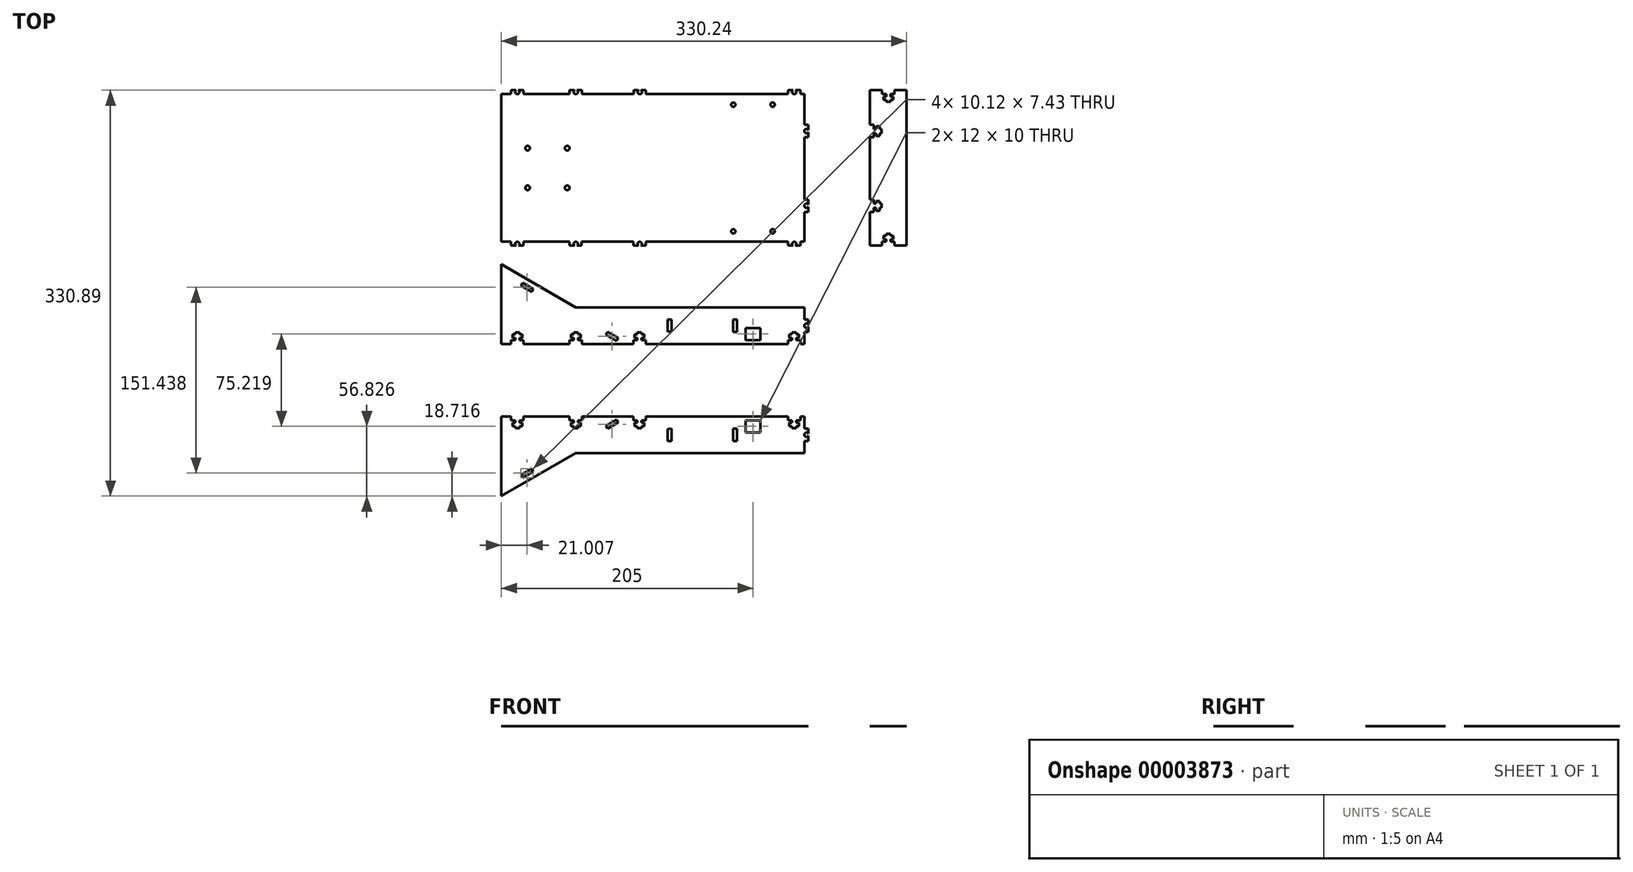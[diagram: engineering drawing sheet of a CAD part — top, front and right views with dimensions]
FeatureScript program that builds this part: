
annotation { "Feature Type Name" : "Feature", "Feature Type Description" : "" }
export const myFeature = defineFeature(function(context is Context, id is Id, definition is map)
    precondition{}
    {
        {
            var Q0;
            Q0=qCreatedBy(makeId("Top.planeOp"),FACE);
            var sketch = newSketch(context, id + "F0", { "sketchPlane" : qUnion([Q0])});
            skLineSegment(sketch, "E0", {"start": v(0, 40.15) * mm, "end": v(0, -39.56) * mm, "construction": true});
            skLineSegment(sketch, "E1", {"start": v(-52.6, 0) * mm, "end": v(51.5, 0) * mm, "construction": true});
            skLineSegment(sketch, "E2", {"start": v(-52.32, -7.62) * mm, "end": v(51.69, -7.62) * mm, "construction": true});
            skLineSegment(sketch, "E3", {"start": v(-7.62, 40.19) * mm, "end": v(-7.62, -39.92) * mm, "construction": true});
            skLineSegment(sketch, "E4", {"start": v(7.62, 39.74) * mm, "end": v(7.62, -40.14) * mm, "construction": true});
            skLineSegment(sketch, "E5", {"start": v(-52.6, 0) * mm, "end": v(-201.44, 0) * mm, "construction": true});
            skLineSegment(sketch, "E6", {"start": v(-52.32, -7.62) * mm, "end": v(-202.66, -7.62) * mm, "construction": true});
            skLineSegment(sketch, "E7", {"start": v(-13.97, 7.62) * mm, "end": v(-17.95, 7.62) * mm});
            skLineSegment(sketch, "E8", {"start": v(-257.62, 10.8) * mm, "end": v(-257.62, 131.12) * mm});
            skLineSegment(sketch, "E9", {"start": v(-7.62, 7.62) * mm, "end": v(-7.62, 10.8) * mm});
            skPoint(sketch, "E10", {"position": v(-97.62, 134.3) * mm});
            skPoint(sketch, "E11", {"position": v(-52.62, 134.3) * mm});
            skPoint(sketch, "E12", {"position": v(-46.62, 134.3) * mm});
            skPoint(sketch, "E13", {"position": v(-58.62, 134.3) * mm});
            skLineSegment(sketch, "E14", {"start": v(-202.66, -7.62) * mm, "end": v(-357.11, -7.62) * mm, "construction": true});
            skLineSegment(sketch, "E15", {"start": v(-201.44, 0) * mm, "end": v(-357.64, 0) * mm, "construction": true});
            skLineSegment(sketch, "E16", {"start": v(-7.62, -39.92) * mm, "end": v(-7.62, -62.62) * mm, "construction": true});
            skLineSegment(sketch, "E17", {"start": v(0, -39.56) * mm, "end": v(0, -201.8) * mm, "construction": true});
            skLineSegment(sketch, "E18", {"start": v(7.62, -40.14) * mm, "end": v(7.62, -202.84) * mm, "construction": true});
            skPoint(sketch, "E19.start.orphan", {"position": v(-257.62, -7.62) * mm});
            skLineSegment(sketch, "E20", {"start": v(-257.62, -7.62) * mm, "end": v(-257.62, -72.62) * mm, "construction": true});
            skLineSegment(sketch, "E21", {"start": v(-257.62, -72.62) * mm, "end": v(-145.04, -72.62) * mm, "construction": true});
            skLineSegment(sketch, "E22", {"start": v(-257.62, -7.62) * mm, "end": v(-197, -42.62) * mm});
            skLineSegment(sketch, "E23", {"start": v(-257.62, -7.62) * mm, "end": v(-257.62, -72.62) * mm});
            skPoint(sketch, "E24", {"position": v(-257.62, -72.62) * mm});
            skPoint(sketch, "E25", {"position": v(-257.62, -42.62) * mm});
            skLineSegment(sketch, "E26", {"start": v(-197, -42.62) * mm, "end": v(-10.8, -42.62) * mm});
            skLineSegment(sketch, "E27", {"start": v(-7.62, -52.62) * mm, "end": v(-7.62, -56.6) * mm});
            skPoint(sketch, "E28", {"position": v(-197, -42.62) * mm});
            skPoint(sketch, "E29", {"position": v(-197, -72.62) * mm});
            skPoint(sketch, "E30", {"position": v(-145.04, -72.62) * mm});
            skLineSegment(sketch, "E31", {"start": v(0, 0) * mm, "end": v(117.44, -117.44) * mm, "construction": true});
            skLineSegment(sketch, "E32", {"start": v(-7.62, -42.62) * mm, "end": v(42.62, -42.62) * mm, "construction": true});
            skLineSegment(sketch, "E33", {"start": v(-7.62, -72.62) * mm, "end": v(72.62, -72.62) * mm});
            skLineSegment(sketch, "E34", {"start": v(-7.62, 134.3) * mm, "end": v(110.23, 134.3) * mm, "construction": true});
            skLineSegment(sketch, "E35", {"start": v(42.62, -42.62) * mm, "end": v(42.62, 134.3) * mm, "construction": true});
            skLineSegment(sketch, "E36", {"start": v(72.62, -72.62) * mm, "end": v(72.62, 134.3) * mm, "construction": true});
            skLineSegment(sketch, "E37", {"start": v(72.62, 7.62) * mm, "end": v(72.62, 134.3) * mm});
            skLineSegment(sketch, "E38", {"start": v(-58.62, 134.3) * mm, "end": v(-58.62, -72.62) * mm, "construction": true});
            skLineSegment(sketch, "E39", {"start": v(-46.62, 134.3) * mm, "end": v(-46.62, -72.62) * mm, "construction": true});
            skPoint(sketch, "E40", {"position": v(-7.62, -57.62) * mm});
            skLineSegment(sketch, "E41", {"start": v(-7.62, -57.62) * mm, "end": v(57.62, -57.62) * mm, "construction": true});
            skLineSegment(sketch, "E42", {"start": v(57.62, -57.62) * mm, "end": v(57.62, 10.8) * mm, "construction": true});
            skPoint(sketch, "E43", {"position": v(-7.62, -52.62) * mm});
            skPoint(sketch, "E44", {"position": v(-7.62, -62.62) * mm});
            skLineSegment(sketch, "E45", {"start": v(-7.62, -52.62) * mm, "end": v(-58.62, -52.62) * mm, "construction": true});
            skLineSegment(sketch, "E46", {"start": v(-7.62, -62.62) * mm, "end": v(-58.62, -62.62) * mm, "construction": true});
            skLineSegment(sketch, "E47", {"start": v(-52.62, 134.3) * mm, "end": v(-52.62, -72.62) * mm, "construction": true});
            skPoint(sketch, "E48", {"position": v(-7.62, -67.62) * mm});
            skLineSegment(sketch, "E49", {"start": v(-7.62, -67.62) * mm, "end": v(-58.62, -67.62) * mm, "construction": true});
            skLineSegment(sketch, "E50", {"start": v(-58.62, -69.45) * mm, "end": v(-58.62, -62.62) * mm});
            skLineSegment(sketch, "E51", {"start": v(-46.62, -62.62) * mm, "end": v(-46.62, -69.45) * mm});
            skLineSegment(sketch, "E52.trimOffspring", {"start": v(-46.62, -72.62) * mm, "end": v(-23.97, -72.62) * mm});
            skLineSegment(sketch, "E53.trimOffspring", {"start": v(-46.62, -72.62) * mm, "end": v(-7.62, -72.62) * mm, "construction": true});
            skPoint(sketch, "E54", {"position": v(-257.62, 7.62) * mm});
            skPoint(sketch, "E55", {"position": v(-257.62, 10.8) * mm});
            skPoint(sketch, "E56", {"position": v(-257.62, 131.12) * mm});
            skLineSegment(sketch, "E57", {"start": v(-257.62, 10.8) * mm, "end": v(-249.62, 10.8) * mm});
            skPoint(sketch, "E58", {"position": v(-249.62, 131.22) * mm});
            skPoint(sketch, "E59", {"position": v(-239.62, 131.13) * mm});
            skPoint(sketch, "E60", {"position": v(-244.62, 131.21) * mm});
            skPoint(sketch, "E61.orphan", {"position": v(-257.62, 134.63) * mm});
            skLineSegment(sketch, "E62.trimOffspring", {"start": v(-58.62, 134.3) * mm, "end": v(-7.62, 134.3) * mm, "construction": true});
            skArc(sketch, "E63", {"start": v(-245.64, 134.39) * mm, "mid": v(-244.63, 131.21) * mm, "end": v(-243.6, 134.38) * mm});
            skArc(sketch, "E64", {"start": v(-143.9, 7.62) * mm, "mid": v(-144.93, 10.8) * mm, "end": v(-145.95, 7.62) * mm});
            skArc(sketch, "E65", {"start": v(-17.95, 7.62) * mm, "mid": v(-18.97, 10.8) * mm, "end": v(-20, 7.62) * mm});
            skArc(sketch, "E66", {"start": v(-243.6, 7.62) * mm, "mid": v(-244.62, 10.8) * mm, "end": v(-245.64, 7.62) * mm});
            skArc(sketch, "E67", {"start": v(-19.99, 134.3) * mm, "mid": v(-18.96, 131.13) * mm, "end": v(-17.94, 134.3) * mm});
            skArc(sketch, "E68", {"start": v(-145.8, 134.3) * mm, "mid": v(-144.78, 131.13) * mm, "end": v(-143.75, 134.3) * mm});
            skArc(sketch, "E69", {"start": v(-198.02, 134.3) * mm, "mid": v(-197, 131.13) * mm, "end": v(-195.97, 134.3) * mm});
            skPoint(sketch, "E70.start.orphan", {"position": v(-249.62, 134.4) * mm});
            skPoint(sketch, "E71", {"position": v(-197, 131.13) * mm});
            skLineSegment(sketch, "E72", {"start": v(-7.62, 131.13) * mm, "end": v(42.62, 131.13) * mm, "construction": true});
            skLineSegment(sketch, "E73", {"start": v(52.62, 131.13) * mm, "end": v(55.87, 131.13) * mm});
            skLineSegment(sketch, "E74", {"start": v(-195.97, 134.3) * mm, "end": v(-192, 134.3) * mm});
            skPoint(sketch, "E75", {"position": v(-144.78, 131.13) * mm});
            skLineSegment(sketch, "E76", {"start": v(-249.62, 134.4) * mm, "end": v(-245.64, 134.39) * mm});
            skLineSegment(sketch, "E77", {"start": v(-239.62, 131.13) * mm, "end": v(-239.62, 134.38) * mm});
            skLineSegment(sketch, "E78", {"start": v(-239.62, 134.38) * mm, "end": v(-243.6, 134.38) * mm});
            skLineSegment(sketch, "E79", {"start": v(-249.62, 131.22) * mm, "end": v(-249.62, 134.4) * mm});
            skPoint(sketch, "E80", {"position": v(-249.62, 132.8) * mm});
            skLineSegment(sketch, "E81.trimOffspring", {"start": v(-243.6, 134.38) * mm, "end": v(-239.62, 134.38) * mm});
            skLineSegment(sketch, "E82.trimOffspring", {"start": v(-245.64, 134.39) * mm, "end": v(-249.62, 134.4) * mm});
            skPoint(sketch, "E83", {"position": v(-192, 131.25) * mm});
            skPoint(sketch, "E84", {"position": v(-202, 131.13) * mm});
            skLineSegment(sketch, "E85", {"start": v(-192, 131.25) * mm, "end": v(-192, 134.3) * mm});
            skLineSegment(sketch, "E86", {"start": v(-192, 134.3) * mm, "end": v(-195.97, 134.3) * mm});
            skLineSegment(sketch, "E87", {"start": v(-202, 131.13) * mm, "end": v(-202, 134.3) * mm});
            skLineSegment(sketch, "E88", {"start": v(-202, 134.3) * mm, "end": v(-198.02, 134.3) * mm});
            skLineSegment(sketch, "E89", {"start": v(-197, 132.88) * mm, "end": v(-197, 132.88) * mm});
            skLineSegment(sketch, "E90.trimOffspring", {"start": v(-197, 132.88) * mm, "end": v(-197, 134.3) * mm, "construction": true});
            skPoint(sketch, "E91", {"position": v(-13.97, 131.13) * mm});
            skPoint(sketch, "E92", {"position": v(-23.97, 131.13) * mm});
            skPoint(sketch, "E93", {"position": v(-18.97, 131.13) * mm});
            skLineSegment(sketch, "E94", {"start": v(-23.97, 131.13) * mm, "end": v(-23.97, 134.3) * mm});
            skLineSegment(sketch, "E95", {"start": v(-13.97, 131.13) * mm, "end": v(-13.97, 134.3) * mm});
            skLineSegment(sketch, "E96", {"start": v(-23.97, 134.3) * mm, "end": v(-19.99, 134.3) * mm});
            skLineSegment(sketch, "E97.trimOffspring", {"start": v(-17.94, 134.3) * mm, "end": v(-13.97, 134.3) * mm});
            skPoint(sketch, "E98", {"position": v(-149.78, 131.16) * mm});
            skPoint(sketch, "E99", {"position": v(-139.78, 131.13) * mm});
            skLineSegment(sketch, "E100", {"start": v(-149.78, 131.16) * mm, "end": v(-149.78, 134.3) * mm});
            skLineSegment(sketch, "E101", {"start": v(-139.78, 131.13) * mm, "end": v(-139.78, 134.3) * mm});
            skLineSegment(sketch, "E102", {"start": v(-139.78, 134.3) * mm, "end": v(-143.75, 134.3) * mm});
            skLineSegment(sketch, "E103.trimOffspring", {"start": v(-145.8, 134.3) * mm, "end": v(-149.78, 134.3) * mm});
            skLineSegment(sketch, "E104", {"start": v(-143.75, 134.3) * mm, "end": v(-139.78, 134.3) * mm});
            skLineSegment(sketch, "E105", {"start": v(-139.78, 134.3) * mm, "end": v(-139.78, 131.13) * mm});
            skPoint(sketch, "E106", {"position": v(-145.8, 134.3) * mm});
            skPoint(sketch, "E107", {"position": v(-143.75, 134.3) * mm});
            skPoint(sketch, "E108.end.orphan", {"position": v(-144.77, 134.3) * mm});
            skLineSegment(sketch, "E109", {"start": v(-257.62, 131.12) * mm, "end": v(-249.62, 131.22) * mm});
            skLineSegment(sketch, "E110", {"start": v(-239.62, 131.13) * mm, "end": v(-202, 131.13) * mm});
            skLineSegment(sketch, "E111", {"start": v(-192, 131.25) * mm, "end": v(-149.78, 131.16) * mm});
            skLineSegment(sketch, "E112", {"start": v(-139.78, 131.13) * mm, "end": v(-23.97, 131.13) * mm});
            skLineSegment(sketch, "E113", {"start": v(-13.97, 131.13) * mm, "end": v(-10.8, 131.13) * mm});
            skLineSegment(sketch, "E114", {"start": v(-249.62, 7.62) * mm, "end": v(-249.62, 10.8) * mm});
            skLineSegment(sketch, "E115", {"start": v(-249.62, 7.62) * mm, "end": v(-245.64, 7.62) * mm});
            skLineSegment(sketch, "E116", {"start": v(-239.62, 7.62) * mm, "end": v(-239.62, 10.8) * mm});
            skLineSegment(sketch, "E117.trimOffspring", {"start": v(-239.62, 10.8) * mm, "end": v(-202, 10.8) * mm});
            skLineSegment(sketch, "E118", {"start": v(-202, 7.62) * mm, "end": v(-198.02, 7.62) * mm});
            skLineSegment(sketch, "E119", {"start": v(-202, 7.62) * mm, "end": v(-202, 10.8) * mm});
            skLineSegment(sketch, "E120.trimOffspring", {"start": v(-239.62, 7.62) * mm, "end": v(-243.6, 7.62) * mm});
            skLineSegment(sketch, "E121", {"start": v(-192.26, 7.62) * mm, "end": v(-192.25, 10.8) * mm});
            skLineSegment(sketch, "E122.trimOffspring", {"start": v(-192.25, 10.8) * mm, "end": v(-150.03, 10.8) * mm});
            skLineSegment(sketch, "E123", {"start": v(-150.04, 7.62) * mm, "end": v(-150.03, 10.8) * mm});
            skLineSegment(sketch, "E124", {"start": v(-139.78, 7.62) * mm, "end": v(-139.78, 10.8) * mm});
            skLineSegment(sketch, "E125.trimOffspring", {"start": v(-192.26, 7.62) * mm, "end": v(-195.97, 7.62) * mm});
            skLineSegment(sketch, "E126.trimOffspring", {"start": v(-139.78, 10.8) * mm, "end": v(-58.62, 10.8) * mm});
            skLineSegment(sketch, "E127.trimOffspring", {"start": v(-52.62, 10.8) * mm, "end": v(-7.62, 10.8) * mm});
            skLineSegment(sketch, "E128", {"start": v(-58.62, 10.8) * mm, "end": v(-46.62, 10.8) * mm});
            skLineSegment(sketch, "E129.trimOffspring", {"start": v(-52.23, 7.62) * mm, "end": v(-52.62, 7.62) * mm});
            skLineSegment(sketch, "E130", {"start": v(-23.97, 7.62) * mm, "end": v(-23.97, 10.8) * mm});
            skLineSegment(sketch, "E131", {"start": v(-13.97, 7.62) * mm, "end": v(-13.97, 10.8) * mm});
            skPoint(sketch, "E132", {"position": v(-18.97, 10.8) * mm});
            skLineSegment(sketch, "E133", {"start": v(-144.93, 9.04) * mm, "end": v(-144.93, 7.29) * mm});
            skPoint(sketch, "E134", {"position": v(-244.62, 10.8) * mm});
            skLineSegment(sketch, "E135.trimOffspring", {"start": v(-245.64, 7.62) * mm, "end": v(-249.62, 7.62) * mm});
            skLineSegment(sketch, "E136.trimOffspring", {"start": v(-243.6, 7.62) * mm, "end": v(-239.62, 7.62) * mm});
            skLineSegment(sketch, "E137", {"start": v(-144.93, 9.04) * mm, "end": v(-144.93, 10.8) * mm});
            skArc(sketch, "E138", {"start": v(-195.97, 7.62) * mm, "mid": v(-197, 10.8) * mm, "end": v(-198.02, 7.62) * mm});
            skArc(sketch, "E139", {"start": v(-7.62, 41.22) * mm, "mid": v(-10.8, 40.2) * mm, "end": v(-7.62, 39.17) * mm});
            skArc(sketch, "E140", {"start": v(-7.62, -56.6) * mm, "mid": v(-10.8, -57.62) * mm, "end": v(-7.62, -58.64) * mm});
            skArc(sketch, "E141", {"start": v(-7.62, 102.07) * mm, "mid": v(-10.8, 101.04) * mm, "end": v(-7.62, 100.02) * mm});
            skLineSegment(sketch, "E142.trimOffspring", {"start": v(-198.02, 7.62) * mm, "end": v(-202, 7.62) * mm});
            skLineSegment(sketch, "E143.trimOffspring", {"start": v(-195.97, 7.62) * mm, "end": v(-192.26, 7.62) * mm});
            skLineSegment(sketch, "E144.trimOffspring", {"start": v(-144.93, 7.62) * mm, "end": v(-144.93, 7.62) * mm});
            skLineSegment(sketch, "E145.trimOffspring", {"start": v(-143.9, 7.62) * mm, "end": v(-139.78, 7.62) * mm});
            skArc(sketch, "E146.trimOffspring", {"start": v(-144.93, 7.29) * mm, "mid": v(-144.93, 7.29) * mm, "end": v(-144.93, 7.29) * mm});
            skLineSegment(sketch, "E147", {"start": v(-150.04, 7.62) * mm, "end": v(-145.95, 7.62) * mm});
            skLineSegment(sketch, "E148.trimOffspring", {"start": v(-20, 7.62) * mm, "end": v(-23.97, 7.62) * mm});
            skLineSegment(sketch, "E149.trimOffspring", {"start": v(-18.97, 7.62) * mm, "end": v(-13.97, 7.62) * mm});
            skPoint(sketch, "E150", {"position": v(-10.8, 131.13) * mm});
            skLineSegment(sketch, "E151", {"start": v(-10.8, 131.13) * mm, "end": v(-10.8, 10.8) * mm});
            skPoint(sketch, "E152", {"position": v(-257.62, 40.88) * mm});
            skPoint(sketch, "E153", {"position": v(-257.7, 70.96) * mm});
            skPoint(sketch, "E154", {"position": v(-257.62, 101.04) * mm});
            skLineSegment(sketch, "E155", {"start": v(-7.62, 40.19) * mm, "end": v(42.62, 39.91) * mm, "construction": true});
            skPoint(sketch, "E156", {"position": v(-7.62, 106.04) * mm});
            skPoint(sketch, "E157", {"position": v(-7.62, 96.04) * mm});
            skLineSegment(sketch, "E158", {"start": v(-7.62, 106.04) * mm, "end": v(-10.8, 106.04) * mm});
            skLineSegment(sketch, "E159", {"start": v(-7.62, 96.04) * mm, "end": v(-10.8, 96.04) * mm});
            skPoint(sketch, "E160", {"position": v(-7.62, 45.19) * mm});
            skPoint(sketch, "E161", {"position": v(-7.62, 101.04) * mm});
            skPoint(sketch, "E162", {"position": v(-7.62, 35.19) * mm});
            skLineSegment(sketch, "E163", {"start": v(-7.62, 45.19) * mm, "end": v(-10.8, 45.19) * mm});
            skLineSegment(sketch, "E164", {"start": v(-7.62, 35.19) * mm, "end": v(-10.8, 35.19) * mm});
            skPoint(sketch, "E165", {"position": v(-10.8, 45.19) * mm});
            skPoint(sketch, "E166", {"position": v(-10.8, 35.19) * mm});
            skPoint(sketch, "E167", {"position": v(-10.8, 101.04) * mm});
            skLineSegment(sketch, "E168.trimOffspring", {"start": v(-7.62, 96.04) * mm, "end": v(-7.62, 100.02) * mm});
            skLineSegment(sketch, "E169.trimOffspring", {"start": v(-7.62, 35.19) * mm, "end": v(-7.62, 39.17) * mm});
            skLineSegment(sketch, "E170.trimOffspring", {"start": v(-7.62, 102.07) * mm, "end": v(-7.62, 106.04) * mm});
            skLineSegment(sketch, "E171.trimOffspring", {"start": v(-7.62, 41.22) * mm, "end": v(-7.62, 45.19) * mm});
            skLineSegment(sketch, "E172", {"start": v(-144.78, 132.88) * mm, "end": v(-143.02, 132.88) * mm, "construction": true});
            skLineSegment(sketch, "E173", {"start": v(-144.78, 132.88) * mm, "end": v(-146.53, 132.88) * mm, "construction": true});
            skLineSegment(sketch, "E174", {"start": v(-18.97, 7.62) * mm, "end": v(-18.97, -7.62) * mm, "construction": true});
            skLineSegment(sketch, "E175", {"start": v(-18.97, -7.62) * mm, "end": v(-18.97, -42.62) * mm, "construction": true});
            skLineSegment(sketch, "E176", {"start": v(-18.97, -42.62) * mm, "end": v(-18.97, -72.62) * mm, "construction": true});
            skLineSegment(sketch, "E177", {"start": v(-197, 9.04) * mm, "end": v(-198.75, 9.04) * mm, "construction": true});
            skLineSegment(sketch, "E178", {"start": v(-197, 9.04) * mm, "end": v(-195.25, 9.04) * mm, "construction": true});
            skLineSegment(sketch, "E179", {"start": v(-195.25, 9.04) * mm, "end": v(-195.25, -72.62) * mm, "construction": true});
            skLineSegment(sketch, "E180", {"start": v(-198.75, 9.04) * mm, "end": v(-198.75, -64.68) * mm, "construction": true});
            skLineSegment(sketch, "E181", {"start": v(-244.62, 9.04) * mm, "end": v(-242.87, 9.04) * mm, "construction": true});
            skLineSegment(sketch, "E182", {"start": v(-244.62, 9.04) * mm, "end": v(-246.37, 9.04) * mm, "construction": true});
            skLineSegment(sketch, "E183", {"start": v(-242.87, 9.04) * mm, "end": v(-242.87, -72.62) * mm, "construction": true});
            skLineSegment(sketch, "E184", {"start": v(-244.62, 7.62) * mm, "end": v(-244.62, -67.46) * mm, "construction": true});
            skLineSegment(sketch, "E185", {"start": v(-246.37, 9.04) * mm, "end": v(-246.37, -72.62) * mm, "construction": true});
            skLineSegment(sketch, "E186", {"start": v(-202, 7.62) * mm, "end": v(-202, -63.1) * mm, "construction": true});
            skLineSegment(sketch, "E187", {"start": v(-150.04, 7.62) * mm, "end": v(-150.04, -72.62) * mm, "construction": true});
            skLineSegment(sketch, "E188", {"start": v(-144.93, 9.04) * mm, "end": v(-143.18, 9.04) * mm, "construction": true});
            skLineSegment(sketch, "E189", {"start": v(-144.93, 9.04) * mm, "end": v(-146.68, 9.04) * mm, "construction": true});
            skPoint(sketch, "E190", {"position": v(-143.25, -42.62) * mm});
            skPoint(sketch, "E191", {"position": v(-145, -42.62) * mm});
            skPoint(sketch, "E192", {"position": v(-146.75, -42.62) * mm});
            skLineSegment(sketch, "E193", {"start": v(-143.25, -42.62) * mm, "end": v(-143.28, -72.62) * mm, "construction": true});
            skLineSegment(sketch, "E194", {"start": v(-146.75, -42.62) * mm, "end": v(-146.75, -72.62) * mm, "construction": true});
            skLineSegment(sketch, "E195", {"start": v(-18.97, 9.04) * mm, "end": v(-17.22, 9.04) * mm, "construction": true});
            skLineSegment(sketch, "E196", {"start": v(-18.97, 9.04) * mm, "end": v(-20.72, 9.04) * mm, "construction": true});
            skLineSegment(sketch, "E197", {"start": v(-17.22, -42.62) * mm, "end": v(-17.22, -72.62) * mm, "construction": true});
            skLineSegment(sketch, "E198", {"start": v(-20.72, -42.62) * mm, "end": v(-20.72, -72.62) * mm, "construction": true});
            skLineSegment(sketch, "E199", {"start": v(-23.97, 7.62) * mm, "end": v(-23.97, -72.62) * mm, "construction": true});
            skLineSegment(sketch, "E200", {"start": v(-13.97, 7.62) * mm, "end": v(-13.97, -72.62) * mm, "construction": true});
            skLineSegment(sketch, "E201", {"start": v(-249.62, 7.62) * mm, "end": v(-249.62, -72.62) * mm, "construction": true});
            skLineSegment(sketch, "E202", {"start": v(-9.04, 40.2) * mm, "end": v(-9.04, 41.95) * mm, "construction": true});
            skLineSegment(sketch, "E203", {"start": v(-9.04, 40.2) * mm, "end": v(-9.04, 38.44) * mm, "construction": true});
            skLineSegment(sketch, "E204", {"start": v(-9.04, 101.04) * mm, "end": v(-9.04, 102.8) * mm, "construction": true});
            skLineSegment(sketch, "E205", {"start": v(-9.04, 101.04) * mm, "end": v(-9.04, 99.29) * mm, "construction": true});
            skLineSegment(sketch, "E206", {"start": v(-7.62, 45.19) * mm, "end": v(72.62, 45.19) * mm, "construction": true});
            skLineSegment(sketch, "E207", {"start": v(-9.04, 38.44) * mm, "end": v(72.62, 38.44) * mm, "construction": true});
            skLineSegment(sketch, "E208", {"start": v(-7.62, 35.19) * mm, "end": v(72.62, 35.19) * mm, "construction": true});
            skLineSegment(sketch, "E209", {"start": v(-9.04, 41.95) * mm, "end": v(72.62, 41.95) * mm, "construction": true});
            skLineSegment(sketch, "E210", {"start": v(-9.04, 99.29) * mm, "end": v(72.62, 99.29) * mm, "construction": true});
            skLineSegment(sketch, "E211", {"start": v(-9.04, 102.8) * mm, "end": v(72.62, 102.8) * mm, "construction": true});
            skLineSegment(sketch, "E212", {"start": v(-7.62, 96.04) * mm, "end": v(72.62, 96.04) * mm, "construction": true});
            skLineSegment(sketch, "E213", {"start": v(-7.62, 106.04) * mm, "end": v(72.62, 106.04) * mm, "construction": true});
            skLineSegment(sketch, "E214", {"start": v(-10.8, 10.8) * mm, "end": v(-10.8, -72.62) * mm, "construction": true});
            skLineSegment(sketch, "E215", {"start": v(-7.62, -52.62) * mm, "end": v(-10.8, -52.62) * mm});
            skLineSegment(sketch, "E216", {"start": v(-7.62, -62.62) * mm, "end": v(-10.8, -62.62) * mm});
            skLineSegment(sketch, "E217", {"start": v(-7.62, -57.62) * mm, "end": v(-7.29, -57.62) * mm});
            skLineSegment(sketch, "E218", {"start": v(-10.8, -42.62) * mm, "end": v(-10.8, -52.62) * mm});
            skLineSegment(sketch, "E219", {"start": v(-10.8, -62.62) * mm, "end": v(-10.8, -72.62) * mm});
            skLineSegment(sketch, "E220.trimOffspring", {"start": v(-7.62, -67.62) * mm, "end": v(-7.62, -202.32) * mm, "construction": true});
            skLineSegment(sketch, "E221", {"start": v(-7.62, -58.64) * mm, "end": v(-7.62, -62.62) * mm});
            skPoint(sketch, "E222", {"position": v(-257.58, -69.45) * mm});
            skPoint(sketch, "E223", {"position": v(-257.62, -63.1) * mm});
            skLineSegment(sketch, "E224", {"start": v(-257.62, -63.1) * mm, "end": v(-202, -63.1) * mm, "construction": true});
            skPoint(sketch, "E225", {"position": v(-244.62, -67.46) * mm});
            skPoint(sketch, "E226", {"position": v(-248.59, -67.46) * mm});
            skPoint(sketch, "E227", {"position": v(-240.65, -67.46) * mm});
            skLineSegment(sketch, "E228", {"start": v(-249.62, -72.62) * mm, "end": v(-249.62, -69.46) * mm});
            skLineSegment(sketch, "E229", {"start": v(-249.62, -69.46) * mm, "end": v(-246.37, -69.46) * mm});
            skLineSegment(sketch, "E230", {"start": v(-239.62, -69.47) * mm, "end": v(-242.87, -69.46) * mm});
            skLineSegment(sketch, "E231", {"start": v(-242.87, -69.46) * mm, "end": v(-242.87, -67.46) * mm});
            skLineSegment(sketch, "E232", {"start": v(-246.37, -69.46) * mm, "end": v(-246.37, -67.46) * mm});
            skLineSegment(sketch, "E233", {"start": v(-248.59, -67.46) * mm, "end": v(-248.59, -64.68) * mm});
            skLineSegment(sketch, "E234", {"start": v(-242.87, -67.46) * mm, "end": v(-240.65, -67.46) * mm});
            skLineSegment(sketch, "E235", {"start": v(-240.65, -67.46) * mm, "end": v(-240.65, -64.68) * mm});
            skLineSegment(sketch, "E236", {"start": v(-248.59, -64.68) * mm, "end": v(-246.37, -64.68) * mm});
            skLineSegment(sketch, "E237", {"start": v(-240.65, -64.68) * mm, "end": v(-242.87, -64.68) * mm});
            skLineSegment(sketch, "E238", {"start": v(-242.87, -64.68) * mm, "end": v(-242.87, -63.1) * mm});
            skLineSegment(sketch, "E239", {"start": v(-246.37, -64.68) * mm, "end": v(-246.37, -63.1) * mm});
            skLineSegment(sketch, "E240", {"start": v(-246.37, -63.1) * mm, "end": v(-242.87, -63.1) * mm});
            skLineSegment(sketch, "E241", {"start": v(-246.37, -67.46) * mm, "end": v(-248.59, -67.46) * mm});
            skLineSegment(sketch, "E242", {"start": v(-249.62, -72.62) * mm, "end": v(-257.62, -72.62) * mm});
            skPoint(sketch, "E243", {"position": v(-198.75, -67.46) * mm});
            skLineSegment(sketch, "E244", {"start": v(-198.75, -67.46) * mm, "end": v(-198.75, -69.45) * mm});
            skPoint(sketch, "E245", {"position": v(-200.97, -67.46) * mm});
            skPoint(sketch, "E246", {"position": v(-193.03, -67.46) * mm});
            skPoint(sketch, "E247", {"position": v(-197, -67.46) * mm});
            skLineSegment(sketch, "E248", {"start": v(-198.75, -67.46) * mm, "end": v(-200.97, -67.46) * mm});
            skLineSegment(sketch, "E249", {"start": v(-200.97, -67.46) * mm, "end": v(-200.97, -64.68) * mm});
            skLineSegment(sketch, "E250", {"start": v(-200.97, -64.68) * mm, "end": v(-198.75, -64.68) * mm});
            skLineSegment(sketch, "E251", {"start": v(-198.75, -64.68) * mm, "end": v(-198.75, -63.1) * mm});
            skLineSegment(sketch, "E252", {"start": v(-198.75, -63.1) * mm, "end": v(-195.25, -63.1) * mm});
            skLineSegment(sketch, "E253", {"start": v(-195.25, -63.1) * mm, "end": v(-195.25, -64.68) * mm});
            skLineSegment(sketch, "E254", {"start": v(-193.03, -64.68) * mm, "end": v(-195.25, -64.68) * mm});
            skLineSegment(sketch, "E255", {"start": v(-242.87, -64.68) * mm, "end": v(-240.65, -64.68) * mm});
            skLineSegment(sketch, "E256", {"start": v(-240.65, -67.46) * mm, "end": v(-242.87, -67.46) * mm});
            skLineSegment(sketch, "E257", {"start": v(-257.62, -72.62) * mm, "end": v(-249.62, -72.62) * mm});
            skLineSegment(sketch, "E258", {"start": v(-146.75, -63.1) * mm, "end": v(-143.27, -63.1) * mm, "construction": true});
            skLineSegment(sketch, "E259", {"start": v(-143.27, -63.1) * mm, "end": v(-143.27, -64.68) * mm});
            skLineSegment(sketch, "E260", {"start": v(-146.75, -63.1) * mm, "end": v(-146.75, -64.68) * mm, "construction": true});
            skLineSegment(sketch, "E261", {"start": v(-146.75, -69.44) * mm, "end": v(-146.75, -67.46) * mm, "construction": true});
            skLineSegment(sketch, "E262", {"start": v(-139.78, -69.45) * mm, "end": v(-143.28, -69.45) * mm, "construction": true});
            skLineSegment(sketch, "E263", {"start": v(-143.28, -69.45) * mm, "end": v(-143.28, -67.46) * mm, "construction": true});
            skPoint(sketch, "E264", {"position": v(-149, -64.68) * mm});
            skPoint(sketch, "E265", {"position": v(-141.06, -64.68) * mm});
            skPoint(sketch, "E266", {"position": v(-145.03, -64.68) * mm});
            skLineSegment(sketch, "E267", {"start": v(-146.75, -64.68) * mm, "end": v(-149, -64.68) * mm, "construction": true});
            skLineSegment(sketch, "E268", {"start": v(-141.06, -67.46) * mm, "end": v(-143.28, -67.46) * mm, "construction": true});
            skLineSegment(sketch, "E269", {"start": v(-149, -64.68) * mm, "end": v(-149, -67.46) * mm, "construction": true});
            skLineSegment(sketch, "E270", {"start": v(-149, -67.46) * mm, "end": v(-146.75, -67.46) * mm, "construction": true});
            skLineSegment(sketch, "E271.trimOffspring", {"start": v(-140.04, -72.62) * mm, "end": v(-58.62, -72.62) * mm});
            skLineSegment(sketch, "E272.trimOffspring", {"start": v(-143.28, -72.62) * mm, "end": v(-58.62, -72.62) * mm, "construction": true});
            skLineSegment(sketch, "E273", {"start": v(-141.06, -64.68) * mm, "end": v(-143.27, -64.68) * mm, "construction": true});
            skLineSegment(sketch, "E274", {"start": v(-141.06, -64.68) * mm, "end": v(-10.8, -64.68) * mm, "construction": true});
            skLineSegment(sketch, "E275", {"start": v(-141.06, -67.46) * mm, "end": v(-10.8, -67.46) * mm, "construction": true});
            skLineSegment(sketch, "E276", {"start": v(-23.97, -72.62) * mm, "end": v(-23.97, -69.44) * mm});
            skLineSegment(sketch, "E277", {"start": v(-20.72, -63.1) * mm, "end": v(-17.22, -63.1) * mm});
            skLineSegment(sketch, "E278", {"start": v(-17.22, -63.1) * mm, "end": v(-17.22, -64.68) * mm});
            skLineSegment(sketch, "E279", {"start": v(-20.72, -63.1) * mm, "end": v(-20.72, -64.68) * mm});
            skLineSegment(sketch, "E280.trimOffspring", {"start": v(-13.97, -72.62) * mm, "end": v(-10.8, -72.62) * mm});
            skPoint(sketch, "E281", {"position": v(-22.94, -64.68) * mm});
            skPoint(sketch, "E282", {"position": v(-15, -64.67) * mm});
            skLineSegment(sketch, "E283", {"start": v(-22.94, -64.68) * mm, "end": v(-20.72, -64.68) * mm});
            skLineSegment(sketch, "E284", {"start": v(-22.94, -64.68) * mm, "end": v(-22.94, -67.46) * mm});
            skLineSegment(sketch, "E285", {"start": v(-22.94, -67.46) * mm, "end": v(-20.72, -67.46) * mm});
            skLineSegment(sketch, "E286", {"start": v(-15, -64.67) * mm, "end": v(-17.22, -64.68) * mm});
            skLineSegment(sketch, "E287", {"start": v(-15, -64.67) * mm, "end": v(-14.99, -67.46) * mm});
            skLineSegment(sketch, "E288", {"start": v(-14.99, -67.46) * mm, "end": v(-17.22, -67.46) * mm});
            skPoint(sketch, "E289.orphan", {"position": v(-244.62, -72.62) * mm});
            skLineSegment(sketch, "E290.trimOffspring", {"start": v(-198.75, -67.46) * mm, "end": v(-198.75, -72.62) * mm, "construction": true});
            skLineSegment(sketch, "E291.trimOffspring", {"start": v(-23.97, -72.62) * mm, "end": v(-46.62, -72.62) * mm});
            skLineSegment(sketch, "E292.trimOffspring", {"start": v(-242.87, -72.62) * mm, "end": v(-244.62, -72.62) * mm});
            skPoint(sketch, "E293", {"position": v(-46.62, -59.45) * mm});
            skLineSegment(sketch, "E294", {"start": v(-46.62, -62.62) * mm, "end": v(-46.62, -59.45) * mm});
            skLineSegment(sketch, "E295", {"start": v(-46.62, -59.45) * mm, "end": v(-58.62, -59.45) * mm});
            skLineSegment(sketch, "E296", {"start": v(-58.62, -59.45) * mm, "end": v(-58.62, -62.62) * mm});
            skLineSegment(sketch, "E297", {"start": v(-14.99, -67.46) * mm, "end": v(67.62, -67.62) * mm, "construction": true});
            skLineSegment(sketch, "E298", {"start": v(-10.8, -64.68) * mm, "end": v(64.68, -64.68) * mm, "construction": true});
            skLineSegment(sketch, "E299", {"start": v(-17.22, -63.1) * mm, "end": v(63.1, -63.1) * mm, "construction": true});
            skLineSegment(sketch, "E300", {"start": v(-9.04, -57.62) * mm, "end": v(-9.04, -55.87) * mm, "construction": true});
            skLineSegment(sketch, "E301", {"start": v(-9.04, -57.62) * mm, "end": v(-9.04, -59.37) * mm, "construction": true});
            skLineSegment(sketch, "E302", {"start": v(-9.04, -55.87) * mm, "end": v(55.87, -55.87) * mm, "construction": true});
            skLineSegment(sketch, "E303", {"start": v(-9.04, -59.37) * mm, "end": v(59.37, -59.37) * mm, "construction": true});
            skLineSegment(sketch, "E304", {"start": v(-10.8, 10.8) * mm, "end": v(42.62, 10.8) * mm, "construction": true});
            skLineSegment(sketch, "E305", {"start": v(-7.62, -52.62) * mm, "end": v(52.62, -52.62) * mm, "construction": true});
            skLineSegment(sketch, "E306", {"start": v(-7.62, -62.62) * mm, "end": v(62.62, -62.62) * mm, "construction": true});
            skLineSegment(sketch, "E307", {"start": v(52.62, -52.62) * mm, "end": v(52.62, 134.3) * mm, "construction": true});
            skLineSegment(sketch, "E308", {"start": v(55.87, -55.87) * mm, "end": v(55.87, 134.3) * mm, "construction": true});
            skLineSegment(sketch, "E309", {"start": v(59.37, -59.37) * mm, "end": v(59.37, 134.3) * mm, "construction": true});
            skLineSegment(sketch, "E310", {"start": v(62.62, -62.62) * mm, "end": v(62.62, 134.3) * mm, "construction": true});
            skPoint(sketch, "E311.orphan", {"position": v(-189.55, -69.45) * mm});
            skPoint(sketch, "E312", {"position": v(-239.62, -72.62) * mm});
            skLineSegment(sketch, "E313", {"start": v(-239.62, -72.62) * mm, "end": v(-239.62, -69.47) * mm});
            skPoint(sketch, "E314", {"position": v(-192, -72.62) * mm});
            skPoint(sketch, "E315", {"position": v(-202, -72.62) * mm});
            skLineSegment(sketch, "E316", {"start": v(-198.75, -69.45) * mm, "end": v(-202, -69.45) * mm});
            skLineSegment(sketch, "E317", {"start": v(-202, -72.62) * mm, "end": v(-202, -69.45) * mm});
            skLineSegment(sketch, "E318", {"start": v(-202, -69.45) * mm, "end": v(-198.75, -69.45) * mm});
            skLineSegment(sketch, "E319", {"start": v(-195.25, -69.45) * mm, "end": v(-192, -69.45) * mm});
            skLineSegment(sketch, "E320", {"start": v(-192, -72.62) * mm, "end": v(-192, -69.45) * mm});
            skLineSegment(sketch, "E321", {"start": v(-193.03, -67.46) * mm, "end": v(-193.03, -64.68) * mm});
            skLineSegment(sketch, "E322", {"start": v(-193.03, -67.46) * mm, "end": v(-195.25, -67.46) * mm});
            skPoint(sketch, "E323.orphan", {"position": v(-192.8, -64.68) * mm});
            skLineSegment(sketch, "E324", {"start": v(-195.25, -67.46) * mm, "end": v(-195.25, -69.45) * mm});
            skLineSegment(sketch, "E325", {"start": v(-239.62, -72.62) * mm, "end": v(-202, -72.62) * mm});
            skLineSegment(sketch, "E326", {"start": v(-140.04, -72.62) * mm, "end": v(-140.04, -69.45) * mm});
            skLineSegment(sketch, "E327", {"start": v(-140.04, -69.45) * mm, "end": v(-143.28, -69.45) * mm});
            skLineSegment(sketch, "E328", {"start": v(-143.28, -69.45) * mm, "end": v(-143.28, -67.46) * mm});
            skLineSegment(sketch, "E329", {"start": v(-143.28, -67.46) * mm, "end": v(-141.06, -67.46) * mm});
            skLineSegment(sketch, "E330", {"start": v(-141.06, -67.46) * mm, "end": v(-141.06, -64.68) * mm});
            skLineSegment(sketch, "E331", {"start": v(-141.06, -64.68) * mm, "end": v(-143.27, -64.68) * mm});
            skLineSegment(sketch, "E332", {"start": v(-143.27, -63.1) * mm, "end": v(-146.75, -63.1) * mm});
            skLineSegment(sketch, "E333", {"start": v(-146.75, -63.1) * mm, "end": v(-146.75, -64.68) * mm});
            skLineSegment(sketch, "E334", {"start": v(-146.75, -64.68) * mm, "end": v(-149, -64.68) * mm});
            skLineSegment(sketch, "E335", {"start": v(-149, -64.68) * mm, "end": v(-149, -67.46) * mm});
            skLineSegment(sketch, "E336", {"start": v(-149, -67.46) * mm, "end": v(-146.75, -67.46) * mm});
            skLineSegment(sketch, "E337", {"start": v(-146.75, -67.46) * mm, "end": v(-146.75, -69.44) * mm});
            skLineSegment(sketch, "E338", {"start": v(-146.75, -69.44) * mm, "end": v(-150.04, -69.44) * mm});
            skLineSegment(sketch, "E339", {"start": v(-150.04, -72.62) * mm, "end": v(-150.04, -69.44) * mm});
            skLineSegment(sketch, "E340.trimOffspring", {"start": v(0, -69.76) * mm, "end": v(69.76, -69.76) * mm, "construction": true});
            skLineSegment(sketch, "E341", {"start": v(-20.72, -67.46) * mm, "end": v(-20.72, -69.45) * mm});
            skLineSegment(sketch, "E342", {"start": v(-17.22, -67.46) * mm, "end": v(-17.22, -69.45) * mm});
            skLineSegment(sketch, "E343.trimOffspring", {"start": v(-17.22, -69.45) * mm, "end": v(-13.97, -69.45) * mm});
            skLineSegment(sketch, "E344", {"start": v(-13.97, -69.45) * mm, "end": v(-13.97, -72.62) * mm});
            skLineSegment(sketch, "E345", {"start": v(-20.72, -69.45) * mm, "end": v(-23.97, -69.45) * mm});
            skLineSegment(sketch, "E346", {"start": v(-46.62, -72.62) * mm, "end": v(-58.62, -72.62) * mm});
            skLineSegment(sketch, "E347", {"start": v(-46.62, -69.45) * mm, "end": v(-58.62, -69.45) * mm});
            skPoint(sketch, "E348", {"position": v(45.8, 35.19) * mm});
            skPoint(sketch, "E349", {"position": v(47.78, 35.19) * mm});
            skPoint(sketch, "E350", {"position": v(50.56, 35.19) * mm});
            skPoint(sketch, "E351", {"position": v(52.15, 35.19) * mm});
            skPoint(sketch, "E352", {"position": v(42.62, 35.19) * mm});
            skLineSegment(sketch, "E353", {"start": v(45.8, 35.19) * mm, "end": v(45.8, 106.04) * mm, "construction": true});
            skLineSegment(sketch, "E354", {"start": v(47.78, 35.19) * mm, "end": v(47.78, 106.04) * mm, "construction": true});
            skLineSegment(sketch, "E355", {"start": v(50.56, 35.19) * mm, "end": v(50.56, 106.04) * mm, "construction": true});
            skLineSegment(sketch, "E356", {"start": v(52.15, 35.19) * mm, "end": v(52.15, 106.04) * mm, "construction": true});
            skPoint(sketch, "E357", {"position": v(47.78, 43.85) * mm});
            skPoint(sketch, "E358", {"position": v(47.78, 35.91) * mm});
            skPoint(sketch, "E359", {"position": v(47.78, 39.88) * mm});
            skLineSegment(sketch, "E360", {"start": v(42.62, 35.19) * mm, "end": v(45.8, 35.19) * mm});
            skLineSegment(sketch, "E361", {"start": v(45.8, 45.19) * mm, "end": v(42.62, 45.19) * mm});
            skLineSegment(sketch, "E362", {"start": v(47.78, 43.85) * mm, "end": v(50.56, 43.84) * mm});
            skLineSegment(sketch, "E363", {"start": v(50.56, 43.84) * mm, "end": v(50.56, 41.96) * mm});
            skLineSegment(sketch, "E364", {"start": v(47.78, 35.91) * mm, "end": v(50.56, 35.91) * mm});
            skLineSegment(sketch, "E365", {"start": v(52.15, 41.95) * mm, "end": v(52.15, 38.44) * mm});
            skLineSegment(sketch, "E366", {"start": v(47.78, 43.85) * mm, "end": v(47.78, 41.95) * mm});
            skLineSegment(sketch, "E367", {"start": v(47.78, 41.95) * mm, "end": v(45.8, 41.95) * mm});
            skLineSegment(sketch, "E368.trimOffspring", {"start": v(45.8, 41.95) * mm, "end": v(45.8, 45.19) * mm});
            skLineSegment(sketch, "E369", {"start": v(52.15, 41.95) * mm, "end": v(50.56, 41.96) * mm});
            skLineSegment(sketch, "E370", {"start": v(45.8, 35.19) * mm, "end": v(45.8, 38.44) * mm});
            skPoint(sketch, "E371", {"position": v(45.8, 38.44) * mm});
            skLineSegment(sketch, "E372", {"start": v(45.8, 38.44) * mm, "end": v(47.78, 38.44) * mm});
            skLineSegment(sketch, "E373", {"start": v(47.78, 35.91) * mm, "end": v(47.78, 38.44) * mm});
            skLineSegment(sketch, "E374", {"start": v(52.15, 38.44) * mm, "end": v(50.56, 38.44) * mm});
            skLineSegment(sketch, "E375.trimOffspring", {"start": v(42.62, 41.95) * mm, "end": v(42.62, 7.62) * mm});
            skLineSegment(sketch, "E376.trimOffspring", {"start": v(50.56, 39.87) * mm, "end": v(50.56, 35.91) * mm});
            skLineSegment(sketch, "E377.trimOffspring", {"start": v(45.8, 39.9) * mm, "end": v(72.62, 39.74) * mm, "construction": true});
            skLineSegment(sketch, "E378", {"start": v(42.62, 45.19) * mm, "end": v(42.62, 96.04) * mm});
            skPoint(sketch, "E379", {"position": v(47.78, 101.04) * mm});
            skPoint(sketch, "E380", {"position": v(47.78, 105.01) * mm});
            skPoint(sketch, "E381", {"position": v(47.78, 97.07) * mm});
            skPoint(sketch, "E382", {"position": v(62.62, 7.62) * mm});
            skPoint(sketch, "E383", {"position": v(62.62, 12.78) * mm});
            skPoint(sketch, "E384", {"position": v(62.62, 15.56) * mm});
            skPoint(sketch, "E385", {"position": v(62.62, 17.14) * mm});
            skPoint(sketch, "E386", {"position": v(62.62, 19.37) * mm});
            skLineSegment(sketch, "E387", {"start": v(62.62, 7.62) * mm, "end": v(62.62, 10.8) * mm});
            skLineSegment(sketch, "E388", {"start": v(52.62, 7.62) * mm, "end": v(52.62, 10.8) * mm});
            skLineSegment(sketch, "E389", {"start": v(52.62, 10.8) * mm, "end": v(55.87, 10.8) * mm});
            skLineSegment(sketch, "E390", {"start": v(62.62, 10.8) * mm, "end": v(59.37, 10.8) * mm});
            skLineSegment(sketch, "E391.trimOffspring", {"start": v(52.62, 7.62) * mm, "end": v(42.62, 7.62) * mm});
            skLineSegment(sketch, "E392", {"start": v(62.62, 15.56) * mm, "end": v(59.37, 15.56) * mm});
            skLineSegment(sketch, "E393", {"start": v(59.37, 17.14) * mm, "end": v(55.87, 17.14) * mm});
            skLineSegment(sketch, "E394", {"start": v(59.37, 10.8) * mm, "end": v(59.37, 12.78) * mm});
            skLineSegment(sketch, "E395", {"start": v(55.87, 10.8) * mm, "end": v(55.87, 12.78) * mm});
            skPoint(sketch, "E396", {"position": v(53.65, 12.78) * mm});
            skPoint(sketch, "E397", {"position": v(61.59, 12.78) * mm});
            skPoint(sketch, "E398", {"position": v(57.62, 12.78) * mm});
            skLineSegment(sketch, "E399", {"start": v(53.65, 12.78) * mm, "end": v(53.65, 15.56) * mm});
            skPoint(sketch, "E400.orphan", {"position": v(52.62, 12.78) * mm});
            skLineSegment(sketch, "E401", {"start": v(61.59, 12.78) * mm, "end": v(61.59, 15.56) * mm});
            skLineSegment(sketch, "E402", {"start": v(55.87, 17.14) * mm, "end": v(55.87, 15.56) * mm});
            skLineSegment(sketch, "E403", {"start": v(59.37, 17.14) * mm, "end": v(59.37, 15.56) * mm});
            skLineSegment(sketch, "E404.trimOffspring", {"start": v(55.87, 15.56) * mm, "end": v(53.65, 15.56) * mm});
            skLineSegment(sketch, "E405.trimOffspring", {"start": v(57.62, 17.14) * mm, "end": v(57.62, 129.14) * mm, "construction": true});
            skLineSegment(sketch, "E406.trimOffspring", {"start": v(55.87, 12.78) * mm, "end": v(53.65, 12.78) * mm});
            skLineSegment(sketch, "E407.trimOffspring", {"start": v(59.37, 10.8) * mm, "end": v(72.62, 10.8) * mm, "construction": true});
            skLineSegment(sketch, "E408", {"start": v(61.59, 12.78) * mm, "end": v(59.37, 12.78) * mm});
            skLineSegment(sketch, "E409", {"start": v(62.62, 7.62) * mm, "end": v(72.62, 7.62) * mm});
            skLineSegment(sketch, "E410", {"start": v(47.78, 105.01) * mm, "end": v(50.56, 105.01) * mm});
            skLineSegment(sketch, "E411", {"start": v(47.78, 97.07) * mm, "end": v(50.56, 97.07) * mm});
            skLineSegment(sketch, "E412", {"start": v(47.78, 105.01) * mm, "end": v(47.78, 102.8) * mm});
            skLineSegment(sketch, "E413", {"start": v(47.78, 97.07) * mm, "end": v(47.78, 99.29) * mm});
            skLineSegment(sketch, "E414", {"start": v(47.78, 102.8) * mm, "end": v(45.8, 102.8) * mm});
            skLineSegment(sketch, "E415", {"start": v(45.8, 102.8) * mm, "end": v(45.8, 106.04) * mm});
            skLineSegment(sketch, "E416", {"start": v(45.8, 106.04) * mm, "end": v(42.62, 106.04) * mm});
            skLineSegment(sketch, "E417", {"start": v(47.78, 99.29) * mm, "end": v(45.8, 99.29) * mm});
            skLineSegment(sketch, "E418", {"start": v(45.8, 99.29) * mm, "end": v(45.8, 96.04) * mm});
            skLineSegment(sketch, "E419", {"start": v(42.62, 96.04) * mm, "end": v(45.8, 96.04) * mm});
            skLineSegment(sketch, "E420", {"start": v(50.56, 97.07) * mm, "end": v(50.56, 99.29) * mm});
            skLineSegment(sketch, "E421", {"start": v(50.56, 105.01) * mm, "end": v(50.56, 102.8) * mm});
            skLineSegment(sketch, "E422", {"start": v(50.56, 102.8) * mm, "end": v(52.15, 102.8) * mm});
            skLineSegment(sketch, "E423", {"start": v(50.56, 99.29) * mm, "end": v(52.15, 99.29) * mm});
            skLineSegment(sketch, "E424", {"start": v(52.15, 102.8) * mm, "end": v(52.15, 99.29) * mm});
            skLineSegment(sketch, "E425.trimOffspring", {"start": v(42.62, 102.8) * mm, "end": v(42.62, 96.04) * mm});
            skLineSegment(sketch, "E426", {"start": v(42.62, 106.04) * mm, "end": v(42.62, 134.3) * mm});
            skPoint(sketch, "E427", {"position": v(57.62, 129.14) * mm});
            skPoint(sketch, "E428", {"position": v(57.62, 126.36) * mm});
            skPoint(sketch, "E429", {"position": v(57.62, 124.78) * mm});
            skLineSegment(sketch, "E430", {"start": v(52.62, 134.3) * mm, "end": v(52.62, 131.13) * mm});
            skLineSegment(sketch, "E431", {"start": v(62.62, 131.13) * mm, "end": v(62.62, 134.3) * mm});
            skLineSegment(sketch, "E432.trimOffspring", {"start": v(59.37, 131.13) * mm, "end": v(62.62, 131.13) * mm});
            skLineSegment(sketch, "E433", {"start": v(57.62, 124.78) * mm, "end": v(59.37, 124.78) * mm});
            skLineSegment(sketch, "E434", {"start": v(57.62, 124.78) * mm, "end": v(55.87, 124.78) * mm});
            skLineSegment(sketch, "E435", {"start": v(59.37, 131.13) * mm, "end": v(59.37, 129.14) * mm});
            skLineSegment(sketch, "E436", {"start": v(55.87, 129.14) * mm, "end": v(53.65, 129.14) * mm});
            skLineSegment(sketch, "E437", {"start": v(55.87, 129.14) * mm, "end": v(55.87, 131.13) * mm});
            skPoint(sketch, "E438", {"position": v(61.59, 129.14) * mm});
            skPoint(sketch, "E439", {"position": v(53.65, 129.14) * mm});
            skLineSegment(sketch, "E440", {"start": v(61.59, 129.14) * mm, "end": v(61.59, 126.36) * mm});
            skLineSegment(sketch, "E441", {"start": v(59.37, 126.36) * mm, "end": v(61.59, 126.36) * mm});
            skPoint(sketch, "E442.orphan", {"position": v(57.62, 134.3) * mm});
            skLineSegment(sketch, "E443", {"start": v(53.65, 129.14) * mm, "end": v(53.65, 126.36) * mm});
            skLineSegment(sketch, "E444", {"start": v(53.65, 126.36) * mm, "end": v(55.87, 126.36) * mm});
            skLineSegment(sketch, "E445", {"start": v(55.87, 124.78) * mm, "end": v(55.87, 126.36) * mm});
            skLineSegment(sketch, "E446.trimOffspring", {"start": v(62.62, 134.3) * mm, "end": v(72.62, 134.3) * mm});
            skLineSegment(sketch, "E447", {"start": v(59.37, 126.36) * mm, "end": v(59.37, 124.78) * mm});
            skLineSegment(sketch, "E448", {"start": v(52.62, 134.3) * mm, "end": v(42.62, 134.3) * mm});
            skLineSegment(sketch, "E449", {"start": v(61.59, 129.14) * mm, "end": v(59.37, 129.14) * mm});
            skLineSegment(sketch, "E450", {"start": v(0, -102.05) * mm, "end": v(-348.37, -102.05) * mm});
            skLineSegment(sketch, "E451.0.MirrorCS", {"start": v(-257.62, -196.49) * mm, "end": v(-257.62, -131.49) * mm});
            skLineSegment(sketch, "E452.0.MirrorCS", {"start": v(-257.62, -196.49) * mm, "end": v(-197, -161.49) * mm});
            skLineSegment(sketch, "E453.0.MirrorCS", {"start": v(-197, -161.49) * mm, "end": v(-10.8, -161.49) * mm});
            skLineSegment(sketch, "E454.trimOffspring", {"start": v(-149.74, -72.62) * mm, "end": v(-197, -72.62) * mm});
            skLineSegment(sketch, "E455", {"start": v(-192, -72.62) * mm, "end": v(-150.04, -72.62) * mm});
            skLineSegment(sketch, "E456.0.MirrorCS", {"start": v(-10.8, -161.49) * mm, "end": v(-10.8, -151.49) * mm});
            skLineSegment(sketch, "E457.0.MirrorCS", {"start": v(-46.62, -144.66) * mm, "end": v(-58.62, -144.66) * mm});
            skLineSegment(sketch, "E458.0.MirrorCS", {"start": v(-46.62, -141.49) * mm, "end": v(-46.62, -144.66) * mm});
            skLineSegment(sketch, "E459.0.MirrorCS", {"start": v(-46.62, -141.49) * mm, "end": v(-46.62, -134.66) * mm});
            skLineSegment(sketch, "E460.0.MirrorCS", {"start": v(-46.62, -134.66) * mm, "end": v(-58.62, -134.66) * mm});
            skLineSegment(sketch, "E461.0.MirrorCS", {"start": v(-58.62, -134.66) * mm, "end": v(-58.62, -141.49) * mm});
            skLineSegment(sketch, "E462.0.MirrorCS", {"start": v(-58.62, -144.66) * mm, "end": v(-58.62, -141.49) * mm});
            skLineSegment(sketch, "E463.0.MirrorCS", {"start": v(-140.04, -131.49) * mm, "end": v(-140.04, -134.66) * mm});
            skLineSegment(sketch, "E464.0.MirrorCS", {"start": v(-140.04, -134.66) * mm, "end": v(-143.28, -134.66) * mm});
            skLineSegment(sketch, "E465.0.MirrorCS", {"start": v(-143.28, -134.66) * mm, "end": v(-143.28, -136.65) * mm});
            skLineSegment(sketch, "E466.0.MirrorCS", {"start": v(-143.28, -136.65) * mm, "end": v(-141.06, -136.65) * mm});
            skLineSegment(sketch, "E467.0.MirrorCS", {"start": v(-141.06, -136.65) * mm, "end": v(-141.06, -139.43) * mm});
            skLineSegment(sketch, "E468.0.MirrorCS", {"start": v(-141.06, -139.43) * mm, "end": v(-143.27, -139.43) * mm});
            skLineSegment(sketch, "E469.0.MirrorCS", {"start": v(-143.27, -141.01) * mm, "end": v(-143.27, -139.43) * mm});
            skLineSegment(sketch, "E470.0.MirrorCS", {"start": v(-143.27, -141.01) * mm, "end": v(-146.75, -141.01) * mm});
            skLineSegment(sketch, "E471.0.MirrorCS", {"start": v(-146.75, -141.01) * mm, "end": v(-146.75, -139.43) * mm});
            skLineSegment(sketch, "E472.0.MirrorCS", {"start": v(-146.75, -139.43) * mm, "end": v(-149, -139.43) * mm});
            skLineSegment(sketch, "E473.0.MirrorCS", {"start": v(-149, -139.43) * mm, "end": v(-149, -136.65) * mm});
            skLineSegment(sketch, "E474.0.MirrorCS", {"start": v(-149, -136.65) * mm, "end": v(-146.75, -136.65) * mm});
            skLineSegment(sketch, "E475.0.MirrorCS", {"start": v(-146.75, -136.65) * mm, "end": v(-146.75, -134.66) * mm});
            skLineSegment(sketch, "E476.0.MirrorCS", {"start": v(-146.75, -134.66) * mm, "end": v(-150.04, -134.66) * mm});
            skLineSegment(sketch, "E477.0.MirrorCS", {"start": v(-150.04, -131.49) * mm, "end": v(-150.04, -134.66) * mm});
            skLineSegment(sketch, "E478.0.MirrorCS", {"start": v(-192, -131.49) * mm, "end": v(-192, -134.66) * mm});
            skLineSegment(sketch, "E479.0.MirrorCS", {"start": v(-195.25, -134.66) * mm, "end": v(-192, -134.66) * mm});
            skLineSegment(sketch, "E480.0.MirrorCS", {"start": v(-195.25, -136.65) * mm, "end": v(-195.25, -134.66) * mm});
            skLineSegment(sketch, "E481.0.MirrorCS", {"start": v(-193.03, -136.65) * mm, "end": v(-195.25, -136.65) * mm});
            skLineSegment(sketch, "E482.0.MirrorCS", {"start": v(-193.03, -136.65) * mm, "end": v(-193.03, -139.43) * mm});
            skLineSegment(sketch, "E483.0.MirrorCS", {"start": v(-193.03, -139.43) * mm, "end": v(-195.25, -139.43) * mm});
            skLineSegment(sketch, "E484.0.MirrorCS", {"start": v(-195.25, -141.01) * mm, "end": v(-195.25, -139.43) * mm});
            skLineSegment(sketch, "E485.0.MirrorCS", {"start": v(-198.75, -141.01) * mm, "end": v(-195.25, -141.01) * mm});
            skLineSegment(sketch, "E486.0.MirrorCS", {"start": v(-198.75, -139.43) * mm, "end": v(-198.75, -141.01) * mm});
            skLineSegment(sketch, "E487.0.MirrorCS", {"start": v(-200.97, -139.43) * mm, "end": v(-198.75, -139.43) * mm});
            skLineSegment(sketch, "E488.0.MirrorCS", {"start": v(-200.97, -136.65) * mm, "end": v(-200.97, -139.43) * mm});
            skLineSegment(sketch, "E489.0.MirrorCS", {"start": v(-198.75, -136.65) * mm, "end": v(-200.97, -136.65) * mm});
            skLineSegment(sketch, "E490.0.MirrorCS", {"start": v(-198.75, -136.65) * mm, "end": v(-198.75, -134.66) * mm});
            skLineSegment(sketch, "E491.0.MirrorCS", {"start": v(-202, -134.66) * mm, "end": v(-198.75, -134.66) * mm});
            skLineSegment(sketch, "E492.0.MirrorCS", {"start": v(-202, -131.49) * mm, "end": v(-202, -134.66) * mm});
            skLineSegment(sketch, "E493.0.MirrorCS", {"start": v(-239.62, -131.49) * mm, "end": v(-239.62, -134.64) * mm});
            skLineSegment(sketch, "E494.0.MirrorCS", {"start": v(-239.62, -134.64) * mm, "end": v(-242.87, -134.65) * mm});
            skLineSegment(sketch, "E495.0.MirrorCS", {"start": v(-242.87, -134.65) * mm, "end": v(-242.87, -136.65) * mm});
            skLineSegment(sketch, "E496.0.MirrorCS", {"start": v(-240.65, -136.65) * mm, "end": v(-242.87, -136.65) * mm});
            skLineSegment(sketch, "E497.0.MirrorCS", {"start": v(-240.65, -136.65) * mm, "end": v(-240.65, -139.43) * mm});
            skLineSegment(sketch, "E498.0.MirrorCS", {"start": v(-242.87, -139.43) * mm, "end": v(-240.65, -139.43) * mm});
            skLineSegment(sketch, "E499.0.MirrorCS", {"start": v(-242.87, -139.43) * mm, "end": v(-242.87, -141.01) * mm});
            skLineSegment(sketch, "E500.0.MirrorCS", {"start": v(-246.37, -141.01) * mm, "end": v(-242.87, -141.01) * mm});
            skLineSegment(sketch, "E501.0.MirrorCS", {"start": v(-246.37, -139.43) * mm, "end": v(-246.37, -141.01) * mm});
            skLineSegment(sketch, "E502.0.MirrorCS", {"start": v(-248.59, -139.43) * mm, "end": v(-246.37, -139.43) * mm});
            skLineSegment(sketch, "E503.0.MirrorCS", {"start": v(-248.59, -136.65) * mm, "end": v(-248.59, -139.43) * mm});
            skLineSegment(sketch, "E504.0.MirrorCS", {"start": v(-246.37, -136.65) * mm, "end": v(-248.59, -136.65) * mm});
            skLineSegment(sketch, "E505.0.MirrorCS", {"start": v(-249.62, -131.49) * mm, "end": v(-249.62, -134.65) * mm});
            skLineSegment(sketch, "E506.0.MirrorCS", {"start": v(-249.62, -134.65) * mm, "end": v(-246.37, -134.65) * mm});
            skLineSegment(sketch, "E507.0.MirrorCS", {"start": v(-246.37, -134.65) * mm, "end": v(-246.37, -136.65) * mm});
            skLineSegment(sketch, "E508.0.MirrorCS", {"start": v(-7.62, -141.49) * mm, "end": v(-10.8, -141.49) * mm});
            skLineSegment(sketch, "E509.0.MirrorCS", {"start": v(-7.62, -145.47) * mm, "end": v(-7.62, -141.49) * mm});
            skLineSegment(sketch, "E510.0.MirrorCS", {"start": v(-7.62, -151.49) * mm, "end": v(-7.62, -147.51) * mm});
            skLineSegment(sketch, "E511.0.MirrorCS", {"start": v(-7.62, -151.49) * mm, "end": v(-10.8, -151.49) * mm});
            skLineSegment(sketch, "E512.0.MirrorCS", {"start": v(-20.72, -136.65) * mm, "end": v(-20.72, -134.66) * mm});
            skLineSegment(sketch, "E513.0.MirrorCS", {"start": v(-22.94, -136.65) * mm, "end": v(-20.72, -136.65) * mm});
            skLineSegment(sketch, "E514.0.MirrorCS", {"start": v(-22.94, -139.43) * mm, "end": v(-22.94, -136.65) * mm});
            skLineSegment(sketch, "E515.0.MirrorCS", {"start": v(-22.94, -139.43) * mm, "end": v(-20.72, -139.43) * mm});
            skLineSegment(sketch, "E516.0.MirrorCS", {"start": v(-20.72, -141.01) * mm, "end": v(-20.72, -139.43) * mm});
            skLineSegment(sketch, "E517.0.MirrorCS", {"start": v(-20.72, -141.01) * mm, "end": v(-17.22, -141.01) * mm});
            skLineSegment(sketch, "E518.0.MirrorCS", {"start": v(-17.22, -141.01) * mm, "end": v(-17.22, -139.43) * mm});
            skLineSegment(sketch, "E519.0.MirrorCS", {"start": v(-15, -139.44) * mm, "end": v(-14.99, -136.65) * mm});
            skLineSegment(sketch, "E520.0.MirrorCS", {"start": v(-14.99, -136.65) * mm, "end": v(-17.22, -136.65) * mm});
            skLineSegment(sketch, "E521.0.MirrorCS", {"start": v(-17.22, -136.65) * mm, "end": v(-17.22, -134.66) * mm});
            skLineSegment(sketch, "E522.0.MirrorCS", {"start": v(-17.22, -134.66) * mm, "end": v(-13.97, -134.66) * mm});
            skLineSegment(sketch, "E523.0.MirrorCS", {"start": v(-13.97, -134.66) * mm, "end": v(-13.97, -131.49) * mm});
            skLineSegment(sketch, "E524", {"start": v(-17.22, -139.43) * mm, "end": v(-17.22, -141.01) * mm});
            skLineSegment(sketch, "E525.0.MirrorCS", {"start": v(-23.97, -131.49) * mm, "end": v(-23.97, -134.66) * mm});
            skLineSegment(sketch, "E526.0.MirrorCS", {"start": v(-20.72, -134.66) * mm, "end": v(-23.97, -134.66) * mm});
            skLineSegment(sketch, "E527.0.MirrorCS", {"start": v(-10.8, -141.49) * mm, "end": v(-10.8, -131.49) * mm});
            skArc(sketch, "E528.0.MirrorCS", {"start": v(-7.62, -147.51) * mm, "mid": v(-10.8, -146.49) * mm, "end": v(-7.62, -145.47) * mm});
            skLineSegment(sketch, "E529.0.MirrorCS", {"start": v(-15, -139.44) * mm, "end": v(-17.22, -139.43) * mm});
            skPoint(sketch, "E530", {"position": v(-257.62, -12.62) * mm});
            skPoint(sketch, "E531", {"position": v(-257.62, -15.8) * mm});
            skPoint(sketch, "E532", {"position": v(-257.62, -27.14) * mm});
            skPoint(sketch, "E533", {"position": v(-257.62, -30.32) * mm});
            skLineSegment(sketch, "E534", {"start": v(-257.62, -12.62) * mm, "end": v(-153.7, -72.62) * mm, "construction": true});
            skLineSegment(sketch, "E535", {"start": v(-257.62, -15.8) * mm, "end": v(-159.2, -72.62) * mm, "construction": true});
            skLineSegment(sketch, "E536", {"start": v(-257.62, -27.14) * mm, "end": v(-178.86, -72.62) * mm, "construction": true});
            skLineSegment(sketch, "E537", {"start": v(-257.62, -30.32) * mm, "end": v(-184.35, -72.62) * mm, "construction": true});
            skPoint(sketch, "E538", {"position": v(-240.3, -22.62) * mm});
            skPoint(sketch, "E539", {"position": v(-231.55, -27.67) * mm});
            skPoint(sketch, "E540", {"position": v(-205.66, -42.62) * mm});
            skLineSegment(sketch, "E541", {"start": v(-197, -161.49) * mm, "end": v(-257.62, -196.49) * mm});
            skLineSegment(sketch, "E542", {"start": v(-10.8, -151.49) * mm, "end": v(-7.62, -151.49) * mm});
            skLineSegment(sketch, "E543", {"start": v(-7.62, -147.51) * mm, "end": v(-7.62, -151.49) * mm});
            skLineSegment(sketch, "E544", {"start": v(-17.22, -139.43) * mm, "end": v(-15, -139.44) * mm});
            skPoint(sketch, "E545.0.MirrorCS.end.orphan", {"position": v(-257.62, -131.49) * mm});
            skPoint(sketch, "E545.0.MirrorCS.start.orphan", {"position": v(-249.62, -131.49) * mm});
            skPoint(sketch, "E546.end.orphan", {"position": v(-58.62, -131.49) * mm});
            skPoint(sketch, "E546.start.orphan", {"position": v(-46.62, -131.49) * mm});
            skLineSegment(sketch, "E547", {"start": v(-239.62, -131.49) * mm, "end": v(-202, -131.49) * mm});
            skLineSegment(sketch, "E548", {"start": v(-192, -131.49) * mm, "end": v(-150.04, -131.49) * mm});
            skLineSegment(sketch, "E549", {"start": v(-257.62, -131.49) * mm, "end": v(-249.62, -131.49) * mm});
            skLineSegment(sketch, "E550", {"start": v(-10.8, -131.49) * mm, "end": v(-13.97, -131.49) * mm});
            skLineSegment(sketch, "E551", {"start": v(-140.04, -131.49) * mm, "end": v(-23.97, -131.49) * mm});
            skLineSegment(sketch, "E552", {"start": v(-198.75, -134.66) * mm, "end": v(-198.75, -136.65) * mm});
            skLineSegment(sketch, "E553", {"start": v(-240.3, -22.62) * mm, "end": v(-241.67, -25) * mm});
            skLineSegment(sketch, "E554", {"start": v(-231.55, -27.67) * mm, "end": v(-232.93, -30.05) * mm});
            skLineSegment(sketch, "E555", {"start": v(-240.3, -22.62) * mm, "end": v(-231.55, -27.67) * mm});
            skLineSegment(sketch, "E556", {"start": v(-241.67, -25) * mm, "end": v(-232.93, -30.05) * mm});
            skPoint(sketch, "E557", {"position": v(-162.36, -67.62) * mm});
            skPoint(sketch, "E558", {"position": v(-171.1, -62.57) * mm});
            skLineSegment(sketch, "E559", {"start": v(-162.36, -67.62) * mm, "end": v(-171.1, -62.57) * mm});
            skLineSegment(sketch, "E560", {"start": v(-171.1, -62.57) * mm, "end": v(-172.48, -64.95) * mm});
            skLineSegment(sketch, "E561", {"start": v(-162.36, -67.62) * mm, "end": v(-163.73, -70) * mm});
            skLineSegment(sketch, "E562", {"start": v(-172.48, -64.95) * mm, "end": v(-163.73, -70) * mm});
            skLineSegment(sketch, "E563.0.MirrorCS", {"start": v(-240.3, -181.49) * mm, "end": v(-241.67, -179.1) * mm});
            skLineSegment(sketch, "E564.0.MirrorCS", {"start": v(-240.3, -181.49) * mm, "end": v(-231.55, -176.44) * mm});
            skLineSegment(sketch, "E565.0.MirrorCS", {"start": v(-231.55, -176.44) * mm, "end": v(-232.93, -174.06) * mm});
            skLineSegment(sketch, "E566.0.MirrorCS", {"start": v(-241.67, -179.1) * mm, "end": v(-232.93, -174.06) * mm});
            skLineSegment(sketch, "E567.0.MirrorCS", {"start": v(-162.36, -136.49) * mm, "end": v(-171.1, -141.54) * mm});
            skLineSegment(sketch, "E568.0.MirrorCS", {"start": v(-171.1, -141.54) * mm, "end": v(-172.48, -139.16) * mm});
            skLineSegment(sketch, "E569.0.MirrorCS", {"start": v(-172.48, -139.16) * mm, "end": v(-163.73, -134.1) * mm});
            skLineSegment(sketch, "E570.0.MirrorCS", {"start": v(-162.36, -136.49) * mm, "end": v(-163.73, -134.1) * mm});
            skCircle(sketch, "E571", {"center": v(-68.62, 19.3) * mm, "radius": 1.75 * mm});
            skCircle(sketch, "E572", {"center": v(-36.62, 19.3) * mm, "radius": 1.75 * mm});
            skCircle(sketch, "E573", {"center": v(-68.62, 122.63) * mm, "radius": 1.75 * mm});
            skCircle(sketch, "E574", {"center": v(-36.62, 122.63) * mm, "radius": 1.75 * mm});
            skPoint(sketch, "E575", {"position": v(-58.62, 122.63) * mm});
            skPoint(sketch, "E576", {"position": v(-46.62, 122.63) * mm});
            skPoint(sketch, "E577", {"position": v(-118.85, -72.62) * mm});
            skPoint(sketch, "E578", {"position": v(-68.65, -72.62) * mm});
            skLineSegment(sketch, "E579", {"start": v(-58.62, -62.62) * mm, "end": v(-124.69, -62.5) * mm, "construction": true});
            skLineSegment(sketch, "E580", {"start": v(-58.62, -52.62) * mm, "end": v(-125.93, -52.62) * mm, "construction": true});
            skPoint(sketch, "E581", {"position": v(-122.02, -72.62) * mm});
            skPoint(sketch, "E582", {"position": v(-65.47, -72.62) * mm});
            skLineSegment(sketch, "E583", {"start": v(-68.65, -62.6) * mm, "end": v(-68.65, -52.62) * mm});
            skLineSegment(sketch, "E584", {"start": v(-65.47, -62.6) * mm, "end": v(-65.47, -52.62) * mm});
            skLineSegment(sketch, "E585", {"start": v(-122.02, -62.5) * mm, "end": v(-122.02, -52.62) * mm});
            skLineSegment(sketch, "E586", {"start": v(-118.85, -62.5) * mm, "end": v(-118.85, -52.62) * mm});
            skLineSegment(sketch, "E587", {"start": v(-122.02, -62.5) * mm, "end": v(-118.85, -62.5) * mm});
            skLineSegment(sketch, "E588", {"start": v(-122.02, -52.62) * mm, "end": v(-118.85, -52.62) * mm});
            skLineSegment(sketch, "E589", {"start": v(-68.65, -62.6) * mm, "end": v(-65.47, -62.6) * mm});
            skLineSegment(sketch, "E590", {"start": v(-68.65, -52.62) * mm, "end": v(-65.47, -52.62) * mm});
            skLineSegment(sketch, "E591.0.MirrorCS", {"start": v(-122.02, -141.61) * mm, "end": v(-122.02, -151.49) * mm});
            skLineSegment(sketch, "E592.0.MirrorCS", {"start": v(-122.02, -151.49) * mm, "end": v(-118.85, -151.49) * mm});
            skLineSegment(sketch, "E593.0.MirrorCS", {"start": v(-118.85, -141.6) * mm, "end": v(-118.85, -151.49) * mm});
            skLineSegment(sketch, "E594.0.MirrorCS", {"start": v(-122.02, -141.61) * mm, "end": v(-118.85, -141.6) * mm});
            skLineSegment(sketch, "E595.0.MirrorCS", {"start": v(-68.65, -141.5) * mm, "end": v(-68.65, -151.49) * mm});
            skLineSegment(sketch, "E596.0.MirrorCS", {"start": v(-68.65, -151.49) * mm, "end": v(-65.47, -151.49) * mm});
            skLineSegment(sketch, "E597.0.MirrorCS", {"start": v(-65.47, -141.5) * mm, "end": v(-65.47, -151.49) * mm});
            skLineSegment(sketch, "E598.0.MirrorCS", {"start": v(-68.65, -141.5) * mm, "end": v(-65.47, -141.5) * mm});
            skPoint(sketch, "E599", {"position": v(-240.26, 70.96) * mm});
            skPoint(sketch, "E600", {"position": v(-240.26, 91.13) * mm});
            skPoint(sketch, "E601", {"position": v(-240.26, 50.79) * mm});
            skPoint(sketch, "E602", {"position": v(-199.92, 91.13) * mm});
            skPoint(sketch, "E603", {"position": v(-199.92, 50.79) * mm});
            skPoint(sketch, "E604", {"position": v(-236.23, 91.13) * mm});
            skPoint(sketch, "E605", {"position": v(-236.23, 50.79) * mm});
            skPoint(sketch, "E606", {"position": v(-240.26, 54.82) * mm});
            skPoint(sketch, "E607", {"position": v(-203.96, 50.79) * mm});
            skPoint(sketch, "E608", {"position": v(-199.92, 54.82) * mm});
            skPoint(sketch, "E609", {"position": v(-203.96, 91.13) * mm});
            skPoint(sketch, "E610", {"position": v(-199.92, 87.1) * mm});
            skPoint(sketch, "E611", {"position": v(-240.26, 87.1) * mm});
            skPoint(sketch, "E612", {"position": v(-236.23, 54.82) * mm});
            skPoint(sketch, "E613", {"position": v(-203.96, 87.1) * mm});
            skCircle(sketch, "E614", {"center": v(-236.23, 54.82) * mm, "radius": 1.89 * mm});
            skCircle(sketch, "E615", {"center": v(-203.96, 87.1) * mm, "radius": 1.89 * mm});
            skPoint(sketch, "E616", {"position": v(-236.23, 87.1) * mm});
            skCircle(sketch, "E617", {"center": v(-236.23, 87.1) * mm, "radius": 1.89 * mm});
            skPoint(sketch, "E618", {"position": v(-203.96, 54.82) * mm});
            skCircle(sketch, "E619", {"center": v(-203.96, 54.82) * mm, "radius": 1.89 * mm});
            skSolve(sketch);
        }
        {
            var Q0;
            Q0 = qSketchRegion(id + "F0", true);
            extrude(context, id + "F1", {"entities" : qUnion([Q0]), "depth" : 1 / 203.2 * mm});
        }
    });
